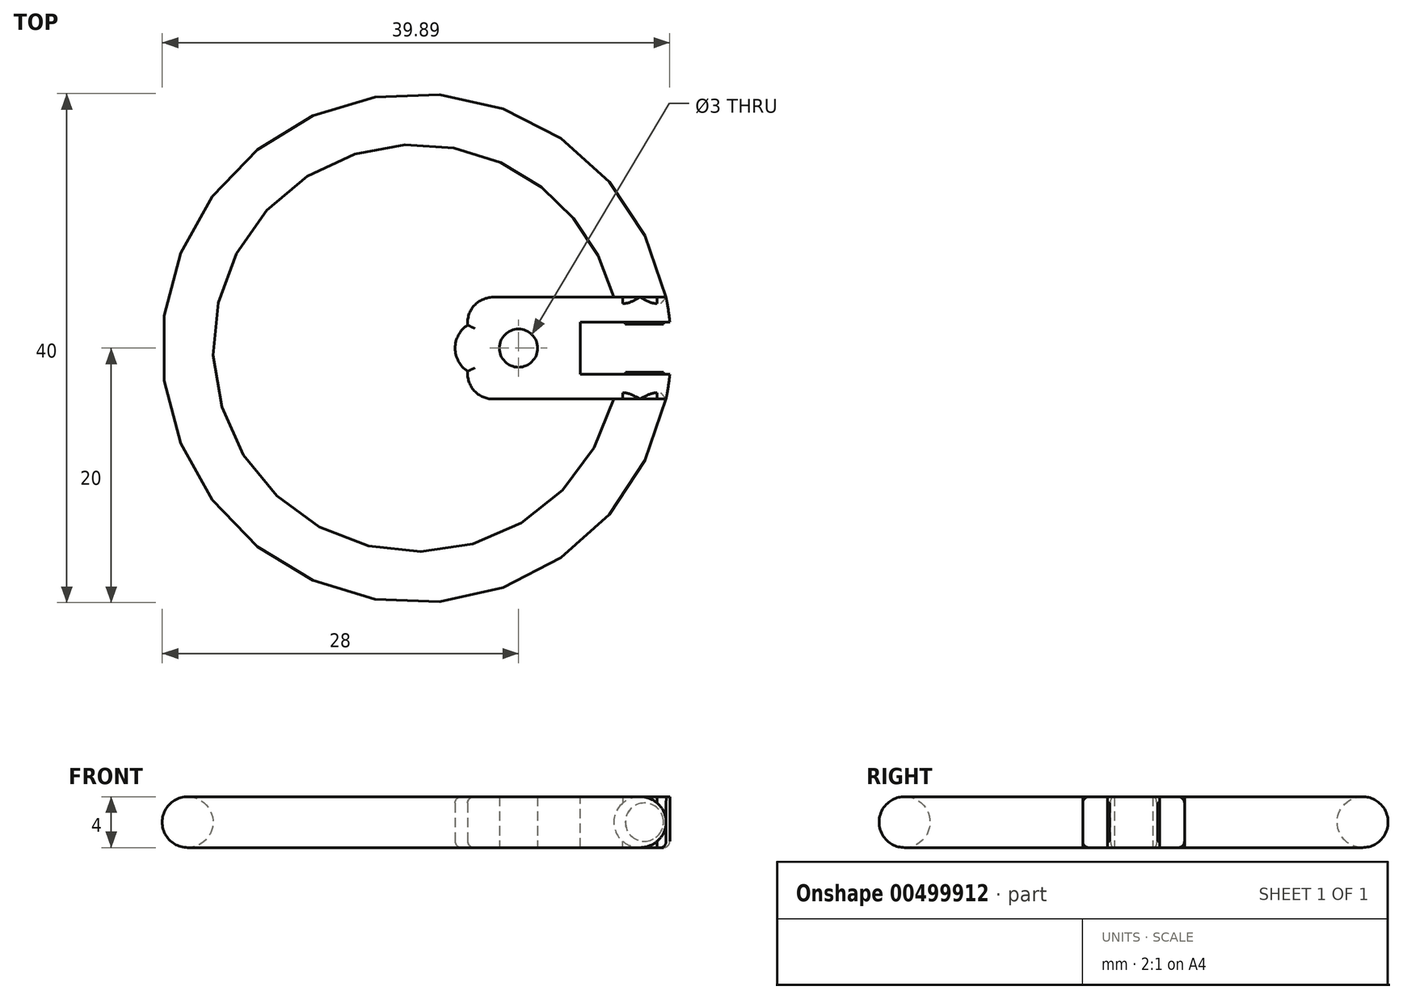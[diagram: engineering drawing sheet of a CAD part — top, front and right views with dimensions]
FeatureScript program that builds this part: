
annotation { "Feature Type Name" : "Feature", "Feature Type Description" : "" }
export const myFeature = defineFeature(function(context is Context, id is Id, definition is map)
    precondition{}
    {
        {
            var Q0;
            Q0=qCreatedBy(makeId("Top.planeOp"),FACE);
            var sketch = newSketch(context, id + "F0", { "sketchPlane" : qUnion([Q0])});
            skCircle(sketch, "E0", {"center": v(0, 0) * mm, "radius": 20 * mm});
            skCircle(sketch, "E1.0", {"center": v(0, 0) * mm, "radius": 16 * mm});
            skSolve(sketch);
        }
        {
            var Q0;
            Q0=qCreatedBy(makeId("Front.planeOp"),FACE);
            var sketch = newSketch(context, id + "F1", { "sketchPlane" : qUnion([Q0])});
            skCircle(sketch, "E2", {"center": v(18, 0) * mm, "radius": 2 * mm});
            skPoint(sketch, "E3.start.orphan", {"position": v(20, 0) * mm});
            skSolve(sketch);
        }
        {
            var Q0;
            Q0=makeQuery(id+"F1.imprint","IMPRINT",FACE,{"disambiguationData":[TD([[makeQuery(id+"F1.imprint","IMPRINT",EDGE,{"derivedFrom":sQuery(id+"F1.wireOp",EDGE,"E2")}),1.0]])]});
            var Q1;
            Q1=sQuery(id+"F0.wireOp",EDGE,"E1.0");
            revolve(context, id + "F2", {"entities" : qUnion([Q0]), "axis" : qUnion([Q1]), "revolveType" : RevolveType.FULL});
        }
        {
            var Q0;
            Q0=qCreatedBy(makeId("Top.planeOp"),FACE);
            var sketch = newSketch(context, id + "F3", { "sketchPlane" : qUnion([Q0])});
            skArc(sketch, "E4", {"start": v(19.6, -4) * mm, "mid": v(20, 0) * mm, "end": v(19.6, 4) * mm});
            skPoint(sketch, "E5.endSnap0", {"position": v(6, 2) * mm});
            skLineSegment(sketch, "E6", {"start": v(6, -4) * mm, "end": v(19.6, -4) * mm});
            skLineSegment(sketch, "E7", {"start": v(6, 4) * mm, "end": v(19.6, 4) * mm});
            skPoint(sketch, "E8.start.orphan", {"position": v(20, 0) * mm});
            skLineSegment(sketch, "E9", {"start": v(19.6, 4) * mm, "end": v(19.6, -4) * mm});
            skArc(sketch, "E10", {"start": v(4, -1.81) * mm, "mid": v(4.52, -3.35) * mm, "end": v(6, -4) * mm});
            skArc(sketch, "E11", {"start": v(6, 4) * mm, "mid": v(4.52, 3.35) * mm, "end": v(4, 1.81) * mm});
            skArc(sketch, "E12", {"start": v(4, 1.81) * mm, "mid": v(3.02, 0) * mm, "end": v(4, -1.81) * mm});
            skPoint(sketch, "E13.orphan", {"position": v(6, 0) * mm});
            skSolve(sketch);
        }
        {
            var Q0;
            Q0 = qSketchRegion(id + "F3", true);
            extrude(context, id + "F4", {"entities" : qUnion([Q0]), "operationType" : NewBodyOperationType.ADD, "depth" : 2 * mm, "hasSecondDirection" : true, "secondDirectionOppositeDirection" : true, "secondDirectionDepth" : 2 * mm});
        }
        {
            var Q0;
            Q0=qCreatedBy(makeId("Right.planeOp"),FACE);
            cPlane(context, id + "F5", {"entities" : qUnion([Q0]), "cplaneType" : CPlaneType.OFFSET, "offset" : 25 * mm, "width" : 150 * mm, "height" : 150 * mm});
        }
        {
            var Q0;
            Q0=qCreatedBy(id+"F5.planeOp",FACE);
            var sketch = newSketch(context, id + "F6", { "sketchPlane" : qUnion([Q0])});
            skLineSegment(sketch, "E14.bottom", {"start": v(2.05, -2) * mm, "end": v(-2.05, -2) * mm});
            skLineSegment(sketch, "E14.top", {"start": v(2.05, 2) * mm, "end": v(-2.05, 2) * mm});
            skLineSegment(sketch, "E14.left", {"start": v(2.05, -2) * mm, "end": v(2.05, 2) * mm});
            skLineSegment(sketch, "E14.right", {"start": v(-2.05, -2) * mm, "end": v(-2.05, 2) * mm});
            skPoint(sketch, "E14.middle", {"position": v(0, 0) * mm});
            skSolve(sketch);
        }
        {
            var Q0;
            Q0 = qSketchRegion(id + "F6", true);
            extrude(context, id + "F7", {"entities" : qUnion([Q0]), "operationType" : NewBodyOperationType.REMOVE, "oppositeDirection" : true, "depth" : 12.15 * mm});
        }
        {
            var Q0;
            Q0=makeQuery(id+"F4.opExtrude","CAP_FACE",FACE,{"disambiguationData":[OSD([sQuery(id+"F3.wireOp",EDGE,"E4"),sQuery(id+"F3.wireOp",EDGE,"E5"),sQuery(id+"F3.wireOp",EDGE,"E6"),sQuery(id+"F3.wireOp",EDGE,"E7")])],"isStart":true});
            var sketch = newSketch(context, id + "F8", { "sketchPlane" : qUnion([Q0])});
            skPoint(sketch, "E15.endSnap0", {"position": v(6, 0) * mm});
            skCircle(sketch, "E16", {"center": v(8, 0) * mm, "radius": 1.5 * mm});
            skPoint(sketch, "E15.start.orphan", {"position": v(12.85, 0) * mm});
            skSolve(sketch);
        }
        {
            var Q0;
            Q0 = qSketchRegion(id + "F8", true);
            extrude(context, id + "F9", {"entities" : qUnion([Q0]), "operationType" : NewBodyOperationType.REMOVE, "oppositeDirection" : true, "depth" : 25 * mm});
        }
        {
            var Q0;
            Q0=makeQuery(id+"F7.boolean.opBoolean","COPY",FACE,{"derivedFrom":makeQuery(id+"F7.opExtrude","SWEPT_FACE",FACE,{"disambiguationData":[OSD([sQuery(id+"F6.wireOp",EDGE,"E14.left")])]})});
            var sketch = newSketch(context, id + "F10", { "sketchPlane" : qUnion([Q0])});
            skLineSegment(sketch, "E17", {"start": v(19.9, 0) * mm, "end": v(17.9, 0) * mm});
            skPoint(sketch, "E17.endSnap0", {"position": v(19.9, 0) * mm});
            skCircle(sketch, "E18", {"center": v(17.9, 0) * mm, "radius": 1.5 * mm});
            skSolve(sketch);
        }
        {
            var Q0;
            Q0 = qSketchRegion(id + "F10", true);
            extrude(context, id + "F11", {"entities" : qUnion([Q0]), "operationType" : NewBodyOperationType.ADD, "depth" : .15 * mm, "offsetDistance" : 25 * mm});
        }
        {
            var Q0;
            Q0=makeQuery(id+"F7.boolean.opBoolean","COPY",FACE,{"derivedFrom":makeQuery(id+"F7.opExtrude","SWEPT_FACE",FACE,{"disambiguationData":[OSD([sQuery(id+"F6.wireOp",EDGE,"E14.right")])]})});
            var sketch = newSketch(context, id + "F12", { "sketchPlane" : qUnion([Q0])});
            skCircle(sketch, "E19", {"center": v(-17.9, 0) * mm, "radius": 1.5 * mm});
            skPoint(sketch, "E20.start.orphan", {"position": v(-19.9, 0) * mm});
            skSolve(sketch);
        }
        {
            var Q0;
            Q0 = qSketchRegion(id + "F12", true);
            extrude(context, id + "F13", {"entities" : qUnion([Q0]), "operationType" : NewBodyOperationType.ADD, "depth" : .15 * mm, "offsetDistance" : 25 * mm});
        }
        {
            var Q0;
            Q0=makeQuery(id+"F4.opExtrude","CAP_EDGE",EDGE,{"disambiguationData":[OSD([sQuery(id+"F3.wireOp",EDGE,"E10")])],"isStart":true});
            var Q1;
            Q1=makeQuery(id+"F4.opExtrude","CAP_EDGE",EDGE,{"disambiguationData":[OSD([sQuery(id+"F3.wireOp",EDGE,"E12")])],"isStart":true});
            var Q2;
            {var subQ0=sQuery(id+"F3.wireOp",EDGE,"E10");var subQ1=sQuery(id+"F3.wireOp",EDGE,"E6");Q2=makeQuery(id+"F4.boolean.opBoolean","SPLIT",EDGE,{"disambiguationData":[TD([makeQuery(id+"F4.opExtrude","SWEPT_FACE",FACE,{"disambiguationData":[OSD([subQ0])]})])],"derivedFrom":makeQuery(id+"F4.opExtrude","CAP_EDGE",EDGE,{"disambiguationData":[OSD([subQ1])],"isStart":true})});}
            var Q3;
            Q3=makeQuery(id+"F4.opExtrude","CAP_EDGE",EDGE,{"disambiguationData":[OSD([sQuery(id+"F3.wireOp",EDGE,"E11")])],"isStart":true});
            var Q4;
            {var subQ0=sQuery(id+"F3.wireOp",EDGE,"E11");var subQ1=sQuery(id+"F3.wireOp",EDGE,"E7");Q4=makeQuery(id+"F4.boolean.opBoolean","SPLIT",EDGE,{"disambiguationData":[TD([makeQuery(id+"F4.opExtrude","SWEPT_FACE",FACE,{"disambiguationData":[OSD([subQ0])]})])],"derivedFrom":makeQuery(id+"F4.opExtrude","CAP_EDGE",EDGE,{"disambiguationData":[OSD([subQ1])],"isStart":true})});}
            var Q5;
            {var subQ0=sQuery(id+"F3.wireOp",EDGE,"E4");var subQ1=sQuery(id+"F3.wireOp",EDGE,"E6");Q5=makeQuery(id+"F4.boolean.opBoolean","SPLIT",EDGE,{"disambiguationData":[TD([makeQuery(id+"F4.opExtrude","SWEPT_FACE",FACE,{"disambiguationData":[OSD([subQ0])]})])],"derivedFrom":makeQuery(id+"F4.opExtrude","CAP_EDGE",EDGE,{"disambiguationData":[OSD([subQ1])],"isStart":true})});}
            var Q6;
            {var subQ0=sQuery(id+"F3.wireOp",EDGE,"E4");var subQ1=sQuery(id+"F3.wireOp",EDGE,"E6");Q6=makeQuery(id+"F7.boolean.opBoolean","SPLIT",EDGE,{"disambiguationData":[TD([makeQuery(id+"F4.opExtrude","SWEPT_FACE",FACE,{"disambiguationData":[OSD([subQ1])]})])],"derivedFrom":makeQuery(id+"F4.opExtrude","CAP_EDGE",EDGE,{"disambiguationData":[OSD([subQ0])],"isStart":true})});}
            var Q7;
            {var subQ0=sQuery(id+"F3.wireOp",EDGE,"E4");var subQ1=sQuery(id+"F3.wireOp",EDGE,"E7");Q7=makeQuery(id+"F7.boolean.opBoolean","SPLIT",EDGE,{"disambiguationData":[TD([makeQuery(id+"F4.opExtrude","SWEPT_FACE",FACE,{"disambiguationData":[OSD([subQ1])]})])],"derivedFrom":makeQuery(id+"F4.opExtrude","CAP_EDGE",EDGE,{"disambiguationData":[OSD([subQ0])],"isStart":true})});}
            var Q8;
            {var subQ0=sQuery(id+"F3.wireOp",EDGE,"E4");var subQ1=sQuery(id+"F3.wireOp",EDGE,"E7");Q8=makeQuery(id+"F4.boolean.opBoolean","SPLIT",EDGE,{"disambiguationData":[TD([makeQuery(id+"F4.opExtrude","SWEPT_FACE",FACE,{"disambiguationData":[OSD([subQ0])]})])],"derivedFrom":makeQuery(id+"F4.opExtrude","CAP_EDGE",EDGE,{"disambiguationData":[OSD([subQ1])],"isStart":true})});}
            var Q9;
            {var subQ0=sQuery(id+"F3.wireOp",EDGE,"E10");var subQ1=sQuery(id+"F3.wireOp",EDGE,"E6");Q9=makeQuery(id+"F4.boolean.opBoolean","SPLIT",EDGE,{"disambiguationData":[TD([makeQuery(id+"F4.opExtrude","SWEPT_FACE",FACE,{"disambiguationData":[OSD([subQ0])]})])],"derivedFrom":makeQuery(id+"F4.opExtrude","CAP_EDGE",EDGE,{"disambiguationData":[OSD([subQ1])],"isStart":false})});}
            var Q10;
            Q10=makeQuery(id+"F4.opExtrude","CAP_EDGE",EDGE,{"disambiguationData":[OSD([sQuery(id+"F3.wireOp",EDGE,"E10")])],"isStart":false});
            var Q11;
            Q11=makeQuery(id+"F4.opExtrude","CAP_EDGE",EDGE,{"disambiguationData":[OSD([sQuery(id+"F3.wireOp",EDGE,"E12")])],"isStart":false});
            var Q12;
            Q12=makeQuery(id+"F4.opExtrude","CAP_EDGE",EDGE,{"disambiguationData":[OSD([sQuery(id+"F3.wireOp",EDGE,"E11")])],"isStart":false});
            var Q13;
            {var subQ0=sQuery(id+"F3.wireOp",EDGE,"E11");var subQ1=sQuery(id+"F3.wireOp",EDGE,"E7");Q13=makeQuery(id+"F4.boolean.opBoolean","SPLIT",EDGE,{"disambiguationData":[TD([makeQuery(id+"F4.opExtrude","SWEPT_FACE",FACE,{"disambiguationData":[OSD([subQ0])]})])],"derivedFrom":makeQuery(id+"F4.opExtrude","CAP_EDGE",EDGE,{"disambiguationData":[OSD([subQ1])],"isStart":false})});}
            fillet(context, id + "F14", {"entities" : qUnion([Q0, Q1, Q2, Q3, Q4, Q5, Q6, Q7, Q8, Q9, Q10, Q11, Q12, Q13]), "radius" : .5 * mm, "tangentPropagation" : true, "allowEdgeOverflow" : false});
        }
    });
